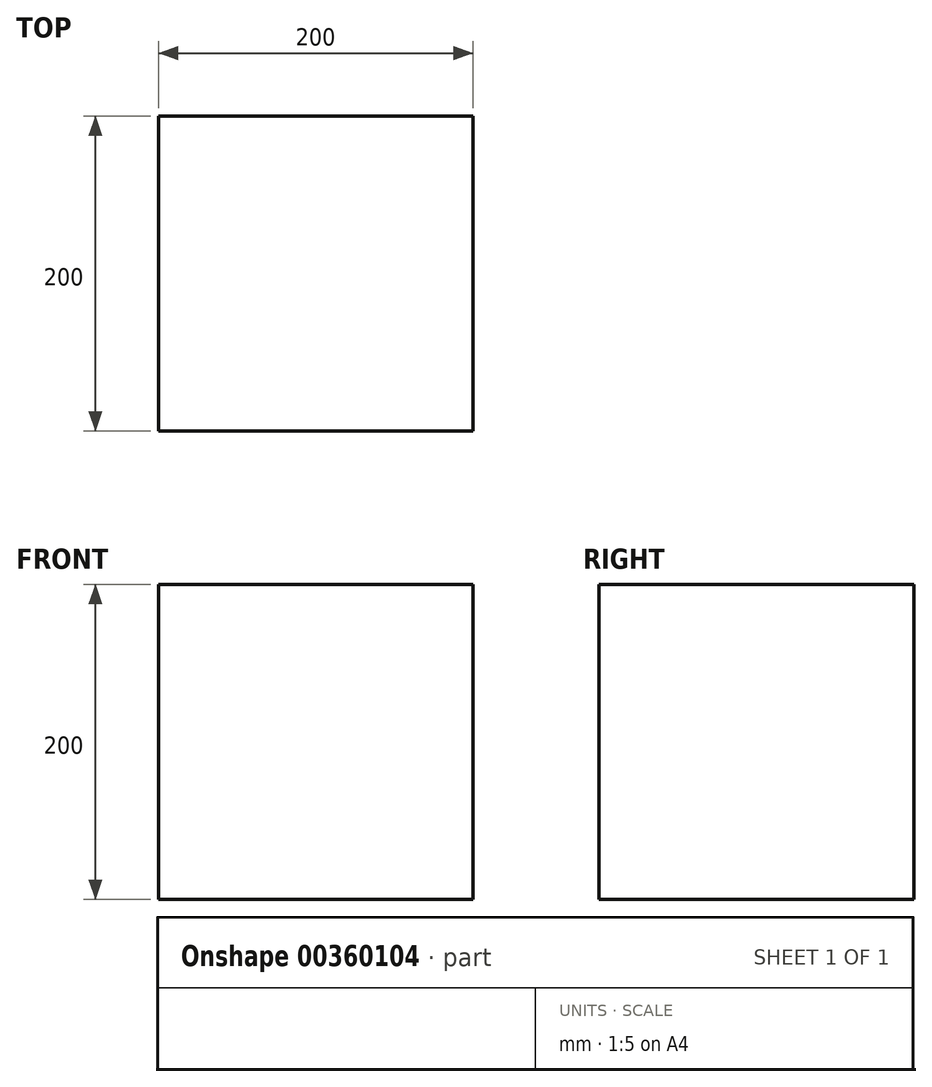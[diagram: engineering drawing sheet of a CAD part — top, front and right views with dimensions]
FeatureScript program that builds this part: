
annotation { "Feature Type Name" : "Feature", "Feature Type Description" : "" }
export const myFeature = defineFeature(function(context is Context, id is Id, definition is map)
    precondition{}
    {
        {
            var Q0;
            Q0=qCreatedBy(makeId("Front.planeOp"),FACE);
            var sketch = newSketch(context, id + "F0", { "sketchPlane" : qUnion([Q0])});
            skLineSegment(sketch, "E0.bottom", {"start": v(-102, -100) * mm, "end": v(98, -100) * mm});
            skLineSegment(sketch, "E0.top", {"start": v(-102, 100) * mm, "end": v(98, 100) * mm});
            skLineSegment(sketch, "E0.left", {"start": v(-102, -100) * mm, "end": v(-102, 100) * mm});
            skLineSegment(sketch, "E0.right", {"start": v(98, -100) * mm, "end": v(98, 100) * mm});
            skPoint(sketch, "E0.middle", {"position": v(-2, 0) * mm});
            skSolve(sketch);
        }
        {
            var Q0;
            Q0 = qSketchRegion(id + "F0", true);
            extrude(context, id + "F1", {"entities" : qUnion([Q0]), "depth" : 200 * mm});
        }
    });
